# Revit family: Electronics_Community-Point-Source_Biamp_Loudspeaker_R_5COAX
name_source: partatom
category: Communication Devices
units: mm (PartAtom-declared; Revit-internal decimal feet)

## family parameters
Cut with Voids When Loaded = No
Host = Face
Maintain Annotation Orientation = No
OmniClass Number = 23.85.10.11.14.14.14
OmniClass Title = Loudspeakers
Part Type = Normal
Room Calculation Point = No
Round Connector Dimension = Use Diameter
Shared = No

## types (4) — shared parameters
Crossover Frequency = 2 kHz
Default Elevation = 48 "
Depth = 15.94 "
Description = R.5COAX 2-Way Coaxial Weather-Resistant Full-Range Loudspeaker
Driver Protection = DYNA-TECH protection circuitry
Drivers = LF 1 x 12 HF 1 x 1 exit titanium free, Ferrofluid-cooled
Enclosure = Rotomolded LLDPE, light grey
Environmental = IEC529 IP54W rating with a minimum 5-degree downward aiming angle
Grill Material = Biamp - Plastic - Gray(Grid)
Grille = 3-layer WeatherStop™, light grey (Zinc-rich epoxy dual-layer powder coated perforated steel grille, foam, woven poly mesh)
Height = 16 "
Housing Material = Biamp - Plastic - Gray
Input Connection = 12 foot (4 m) SJOW #16 gauge
Loudspeaker Type = 2-way, coaxial, weather-resistant, full-range
Manufacturer = Biamp
Max Input Ratings = 200W continuous, 500W program 40 volts RMS, 89 volts momentary peak
Maximum Output on 200W Tap = 125 dB SPL
Mounting/Rigging Provisions = (5) 3/8-16 rigging points
Product Documentation Link = https://downloads.biamp.com
Product Page URL = https://www.biamp.com
Product data url = https://www.bimobject.com
Recommended Power Amplifier = 420W to 600W @ 8 ohms
Required Accessories = 24 dB/Oct high pass filter
URL = https://www.biamp.com
Width = 16 "
Yoke Material = Biamp - Metal - Gray

## per-type parameters (varying)
| type | 200W Nominal Impedance | Axial Q / DI | Connector Description | Controls | Maximum Output | Minimum Impedance | Nominal Impedance | Nominal –6dB Beamwidth | Operating Range | Recommended Signal Processing | Sensitivity (1W/1m) | Weight |
| R.5COAX66 |  | 15.2  / 11.8, 1.6 kHz to 12.5 kHz | Terminal strip; 200W continuous, 500W program, 40 volts RMS, 89 volts momentary peak | None | 121 dB SPL / 128 dB SPL (peak) | 4.2 ohms @ 9.9 kHz | 8 ohms | 60°H (+20° / -6°, 1.6 kHz to 12.5 kHz); 60°V (+20° / -3°, 1.6 kHz to 12.5 kHz) | 80 Hz to 18 kHz 90 Hz to 12.5 kHz (±3.5 dB) | 60 Hz high pass filter | 98 dB SPL (100 Hz to 13 kHz 1/3 octave bands) 97 dB SPL (250 Hz to 4 kHz speech range) | 15.90 kgf |
| R.5COAX66T | 25 Ohms | 15.2  / 11.8, 1.6 kHz to 12.5 kHz | Terminal strip; 70V/100V operation | 4 position autoformer TAP select switch 70V switchable taps @ 200W, 100W, 50W, 25W 100V switchable taps @ 200W, 100W, 50W | 121 dB SPL / 128 dB SPL (peak) | 15.9 Ohms @ 9.8 kHz |  | 60°H (+20° / -6°, 1.6 kHz to 12.5 kHz); 60°V (+20° / -3°, 1.6 kHz to 12.5 kHz) | 80 Hz to 18 kHz 90 Hz to 13 kHz (±3.5 dB) 200 / 100 / 50 / 25 watt autoformer taps @ 70.7V | 80 Hz high pass filter | 97 dB SPL (100 Hz to 13 kHz 1/3 octave bands) 96 dB SPL (250 Hz to 4 kHz speech range) | 17.46 kgf |
| R.5COAX99 |  | 10.7 / 10.3, 1.6 kHz to 12.5 kHz | Terminal strip; 200W continuous, 500W program, 40 volts RMS, 89 volts momentary peak | None | 119 dB SPL / 126 dB SPL (peak) | 3.8 ohms @ 9.9 kHz | 8 ohms | 90°H (+10° / -23°, 1.6 kHz to 12.5 kHz)'; 90°V (+4° / -30°, 1.6 kHz to 12.5 kHz) | 80 Hz to 18 kHz 90 Hz to 12.5 kHz (±3.5 dB) | 60 Hz high pass filter | 96 dB SPL (100 Hz to 13 kHz 1/3 octave bands) 96 dB SPL (250 Hz to 4 kHz speech range) | 15.90 kgf |
| R.5COAX99T | 25 Ohms | 10.7  / 10.3, 1.6 kHz to 12.5 kHz | Terminal strip; 70V/100V operation | 4 position autoformer TAP select switch 70V switchable taps @ 200W, 100W, 50W, 25W 100V switchable taps @ 200W, 100W, 50W | 121 dB SPL / 128 dB SPL (peak) | 15.3 Ohms @ 9.4 kHz |  | 90°H (+10° / -23°, 1.6 kHz to 12.5 kHz); 90°V (+4° / -30°, 1.6 kHz to 12.5 kHz) | 80 Hz to 18 kHz 90 Hz to 13 kHz (±3.5 dB) 200 / 100 / 50 / 25 watt autoformer taps @ 70.7V | 80 Hz high pass filter | 95 dB SPL (100 Hz to 13 kHz 1/3 octave bands) 95 dB SPL (250 Hz to 4 kHz speech range) | 17.46 kgf |

note: column(s) folded — value = type name in every type: Model

## geometry (parser evidence)
native form markers: Sweep x4
no freeform markers — native parametric forms only
